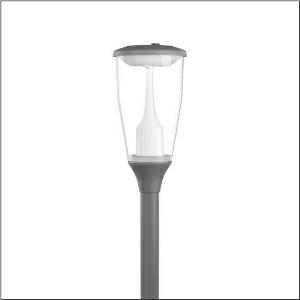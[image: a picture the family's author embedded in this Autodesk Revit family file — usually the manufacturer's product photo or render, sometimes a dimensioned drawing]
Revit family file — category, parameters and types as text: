
# Revit family: dl_11_iq___st1_2a_5xa5575ev14h000022_9f00
name_source: partatom
category: Lighting Fixtures
units: mm (PartAtom-declared; Revit-internal decimal feet)

## family parameters
Cut with Voids When Loaded = No
Host = Face
Light Source = No
Part Type = Normal
Room Calculation Point = No
Round Connector Dimension = Use Diameter
Shared = No

## types (1)
- --- (1 x LED, 1560 lm, 10.7 W, 3000K)
    Apparent Load = 11 VA
    CIE Flux Codes = 24 63 94 96 100
    Color Rendering = 70
    Color Temperature = 3000K
    Default Elevation = 1800 mm
    Description = DL 11 iQ, mast luminaire, Module 540 iQ-SR, primary light control with 3 zone facetted reflector, of plastic, silver coated, highly specular, structured, primary optical cover: cover, of PMMA, transparent, light distribution: ST1.2a, light emission: direct distribution, primary light characteristic: asymmetric, installation type: post-top, LED, High Power LED, rated luminous flux: 1.560lm, luminous efficacy: 146lm/W, light colour: 730, colour temperature: 3000K, control gear: iQ-Street Remote, D4i with power reduction, control: pre-setting: logarithmic dimming characteristic, Street-Remote, Auto-Match, Temp-Guard, Lumen-Switch, Night-Set, Smart-Wire, Light-Fading, Desk-Remote (wireless, voltage-free reading and setting of iQ features in the workshop via application-optimized NFC function/RFID function), optimised constant luminous flux control (CLO 2.0), mains connection: 220..240V, AC, 50/60Hz, connection cable pre-assembled, cable length: 5,5m, start of lifetime: 11W, end of service life: 11W, reduction: 6W, luminaire housing, upper part, of diecast aluminium, coated, SITECO metallic grey (DB 702S), spigot size: 76mm (post-top), mounting height: 3..5m, post-top mast mounting element, of diecast aluminium, coated, SITECO metallic grey (DB 702S), Module 540 iQ-SR, traffic white (RAL 9016), equipment: standard, Smart Interface above, protection rating (complete): IP66, insulation class (complete): insulation class II (safety insulation), certification: CE, ENEC, ENEC+, VDE, impact resistance: IK07, packaging unit: 1 piece

Light Distribution: ST1.2a
    Height = 665 mm
    Lamp = 1 x LED
    Lamp Light Flux = 1560 lm
    Lamp Power = 10.7 W
    Lamp count = 1
    Length = 334 mm
    Luminous efficacy = 146 lm/W
    Manufacturer = Siteco
    ModVariant = No
    Model = 5XA5575EV14H000022
    Number of Poles = 1
    OnlyDefault = Yes
    Power Factor = 1
    Product Name = DL 11 iQ | ST1.2a
    Product group = mast luminaire | pylon top
    ProductGroupID = 6100
    Protection Class = Protection class II
    Protection Degree = IP 66
    RLX_Detail_Level = 1
    RLX_Emergency_Light_Flux = 0 lm
    RLX_Emergency_Type = 0
    RLX_Emergency_Type_DB = No
    RlxData = <blob elided: 155393 chars, md5=b74c0aa9>
    Socket = socket
    Standby Power = 0 W
    System Light Flux = 1560 lm
    System Power = 11 W
    Type Comments = factory setting: luminous flux: 100 % | dim-lin: 254 | 419 mA
    Type Image = l_1337541.jpg
    URL = http://relux.com
    VarID = @adj_098687
    Voltage = 0 V
    Weight = 0.00 kg
    Width = 0 mm  [stored 0 ft]

note: [stored X ft] marks values corroborated as IEEE doubles in the binary element streams (Revit-internal decimal feet)

## geometry (parser evidence)
native form markers: Blend x4, Sweep x8
no freeform markers — native parametric forms only
